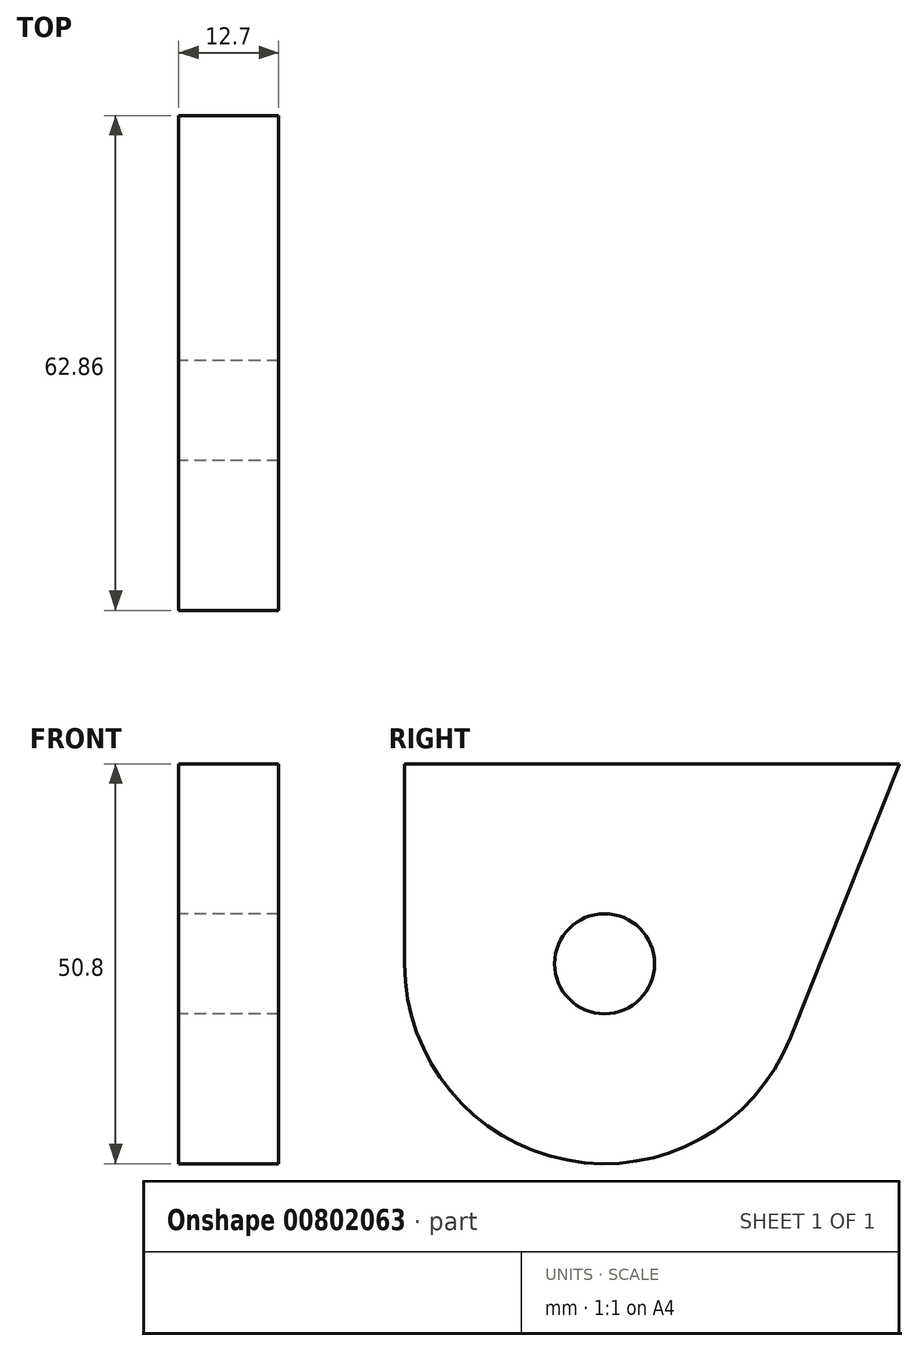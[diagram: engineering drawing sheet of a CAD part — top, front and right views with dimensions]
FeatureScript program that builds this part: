
annotation { "Feature Type Name" : "Feature", "Feature Type Description" : "" }
export const myFeature = defineFeature(function(context is Context, id is Id, definition is map)
    precondition{}
    {
        {
            var Q0;
            Q0=qCreatedBy(makeId("Right.planeOp"),FACE);
            var sketch = newSketch(context, id + "F0", { "sketchPlane" : qUnion([Q0])});
            skCircle(sketch, "E0", {"center": v(0, 0) * mm, "radius": 6.35 * mm});
            skLineSegment(sketch, "E1", {"start": v(-25.4, 25.4) * mm, "end": v(-25.4, 0) * mm});
            skArc(sketch, "E2", {"start": v(-25.4, 0) * mm, "mid": v(-4.78, -24.95) * mm, "end": v(23.6, -9.4) * mm});
            skLineSegment(sketch, "E3", {"start": v(37.46, 25.4) * mm, "end": v(23.6, -9.4) * mm});
            skLineSegment(sketch, "E4", {"start": v(-25.4, 25.4) * mm, "end": v(37.46, 25.4) * mm});
            skSolve(sketch);
        }
        {
            var Q0;
            Q0=qSketchRegion(id+"F0",true);
            extrude(context, id + "F1", {"entities" : qUnion([Q0]), "depth" : 12.7 * mm});
        }
    });
